# Revit family: VUT PB_en
name_source: partatom
category: Оборудование
units: mm (PartAtom-declared; Revit-internal decimal feet)

## family parameters
Всегда вертикально = Да
Классификация = Нет
На основе рабочей плоскости = Нет
Общий = Нет
При загрузке вырезать с полостями = Нет
Размер круглого соединителя = Использовать диаметр
Тип детали = Нормальный
Точка принадлежности помещению = Нет

## types (8) — shared parameters
00_20_Manufacturer = Vents
00_20_Name = Heat recovery air handling unit
Filter = G4, F7
Load Classification = HVAC
Maintenance zone material = <По категории>
Number of Fase = 1
URL = https://ventilation-system.com
Voltage = 230 В
l = 50 мм
Изготовитель = Vents
zero-valued in all types: Отметка по умолчанию

## per-type parameters (varying)
- VUT 160 PB EC L A21: A=500 мм; Amperage=0 А; B=754 мм; Casing Material=Steel, galvanized; D=125 мм; Diameter=125 мм; Dy=120 мм; H=340 мм; Height=340 мм; L=1008 мм; Left=Да; Length=1008 мм; Maximum Air Flow=190.0 м³/ч; Power=50 Вт; Right=Нет; Sound pressure level at 3 m distance=26 dBA; Top mount=Да; Type 180=Нет; Weight=48.00 кг; Width=754 мм; h=-170 мм; h1=20 мм; l2=245 мм; l22=144 мм; l222=245 мм; l3=159 мм; l4=128 мм; l5=123 мм; l6=216 мм
- VUT 160 PB EC R A21: A=500 мм; Amperage=0 А; B=754 мм; Casing Material=Steel, galvanized; D=125 мм; Diameter=125 мм; Dy=120 мм; H=340 мм; Height=340 мм; L=1008 мм; Left=Нет; Length=1008 мм; Maximum Air Flow=190.0 м³/ч; Power=50 Вт; Right=Да; Sound pressure level at 3 m distance=26 dBA; Top mount=Да; Type 180=Нет; Weight=48.00 кг; Width=754 мм; h=-170 мм; h1=20 мм; l2=123 мм; l22=216 мм; l222=216 мм; l3=128 мм; l4=159 мм; l5=245 мм; l6=245 мм
- VUT 250 PB EC R A21: A=500 мм; Amperage=1 А; B=754 мм; Casing Material=Steel, galvanized; D=125 мм; Diameter=125 мм; Dy=120 мм; H=340 мм; Height=340 мм; L=1008 мм; Left=Нет; Length=1008 мм; Maximum Air Flow=270.0 м³/ч; Power=101 Вт; Right=Да; Sound pressure level at 3 m distance=28 dBA; Top mount=Да; Type 180=Нет; Weight=48.00 кг; Width=754 мм; h=-170 мм; h1=20 мм; l2=123 мм; l22=216 мм; l222=216 мм; l3=128 мм; l4=159 мм; l5=245 мм; l6=245 мм
- VUT 250 PB EC L A21: A=500 мм; Amperage=1 А; B=754 мм; Casing Material=Steel, galvanized; D=125 мм; Diameter=125 мм; Dy=120 мм; H=340 мм; Height=340 мм; L=1008 мм; Left=Да; Length=1008 мм; Maximum Air Flow=270.0 м³/ч; Power=101 Вт; Right=Нет; Sound pressure level at 3 m distance=28 dBA; Top mount=Да; Type 180=Нет; Weight=48.00 кг; Width=754 мм; h=-170 мм; h1=20 мм; l2=245 мм; l22=144 мм; l222=245 мм; l3=159 мм; l4=128 мм; l5=123 мм; l6=216 мм
- VUT 350 PB EC L A21: A=700 мм; Amperage=1 А; B=1044 мм; Casing Material=Steel, galvanized; D=160 мм; Diameter=160 мм; Dy=155 мм; H=340 мм; Height=340 мм; L=1138 мм; Left=Да; Length=1138 мм; Maximum Air Flow=410.0 м³/ч; Power=170 Вт; Right=Нет; Sound pressure level at 3 m distance=34 dBA; Top mount=Да; Type 180=Нет; Weight=70.00 кг; Width=1044 мм; h=-170 мм; h1=20 мм; l2=345 мм; l22=144 мм; l222=345 мм; l3=159 мм; l4=119 мм; l5=144 мм; l6=282 мм
- VUT 350 PB EC R A21: A=700 мм; Amperage=1 А; B=1044 мм; Casing Material=Steel, galvanized; D=160 мм; Diameter=160 мм; Dy=155 мм; H=340 мм; Height=340 мм; L=1138 мм; Left=Нет; Length=1138 мм; Maximum Air Flow=410.0 м³/ч; Power=170 Вт; Right=Да; Sound pressure level at 3 m distance=34 dBA; Top mount=Да; Type 180=Нет; Weight=70.00 кг; Width=1044 мм; h=-170 мм; h1=20 мм; l2=144 мм; l22=144 мм; l222=144 мм; l3=119 мм; l4=159 мм; l5=345 мм; l6=345 мм
- VUT 180 P5B EC A21: A=500 мм; Amperage=1 А; B=600 мм; Casing Material=Polypropylene (black); D=150 мм; Diameter=150 мм; Dy=145 мм; H=264 мм; Height=264 мм; L=900 мм; Left=Нет; Length=900 мм; Maximum Air Flow=220.0 м³/ч; Power=87 Вт; Right=Нет; Sound pressure level at 3 m distance=33 dBA; Top mount=Нет; Type 180=Да; Weight=14.00 кг; Width=600 мм; h=-132 мм; h1=0 мм; l2=137 мм; l22=144 мм; l222=137 мм; l3=132 мм; l4=132 мм; l5=137 мм; l6=137 мм
- VUE 180 P5B EC A21: A=500 мм; Amperage=1 А; B=600 мм; Casing Material=Polypropylene (black); D=150 мм; Diameter=150 мм; Dy=145 мм; H=264 мм; Height=264 мм; L=900 мм; Left=Нет; Length=900 мм; Maximum Air Flow=220.0 м³/ч; Power=87 Вт; Right=Нет; Sound pressure level at 3 m distance=33 dBA; Top mount=Нет; Type 180=Да; Weight=14.00 кг; Width=600 мм; h=-132 мм; h1=0 мм; l2=137 мм; l22=144 мм; l222=137 мм; l3=132 мм; l4=132 мм; l5=137 мм; l6=137 мм

note: column(s) folded — value = type name in every type: 00_20_Type
